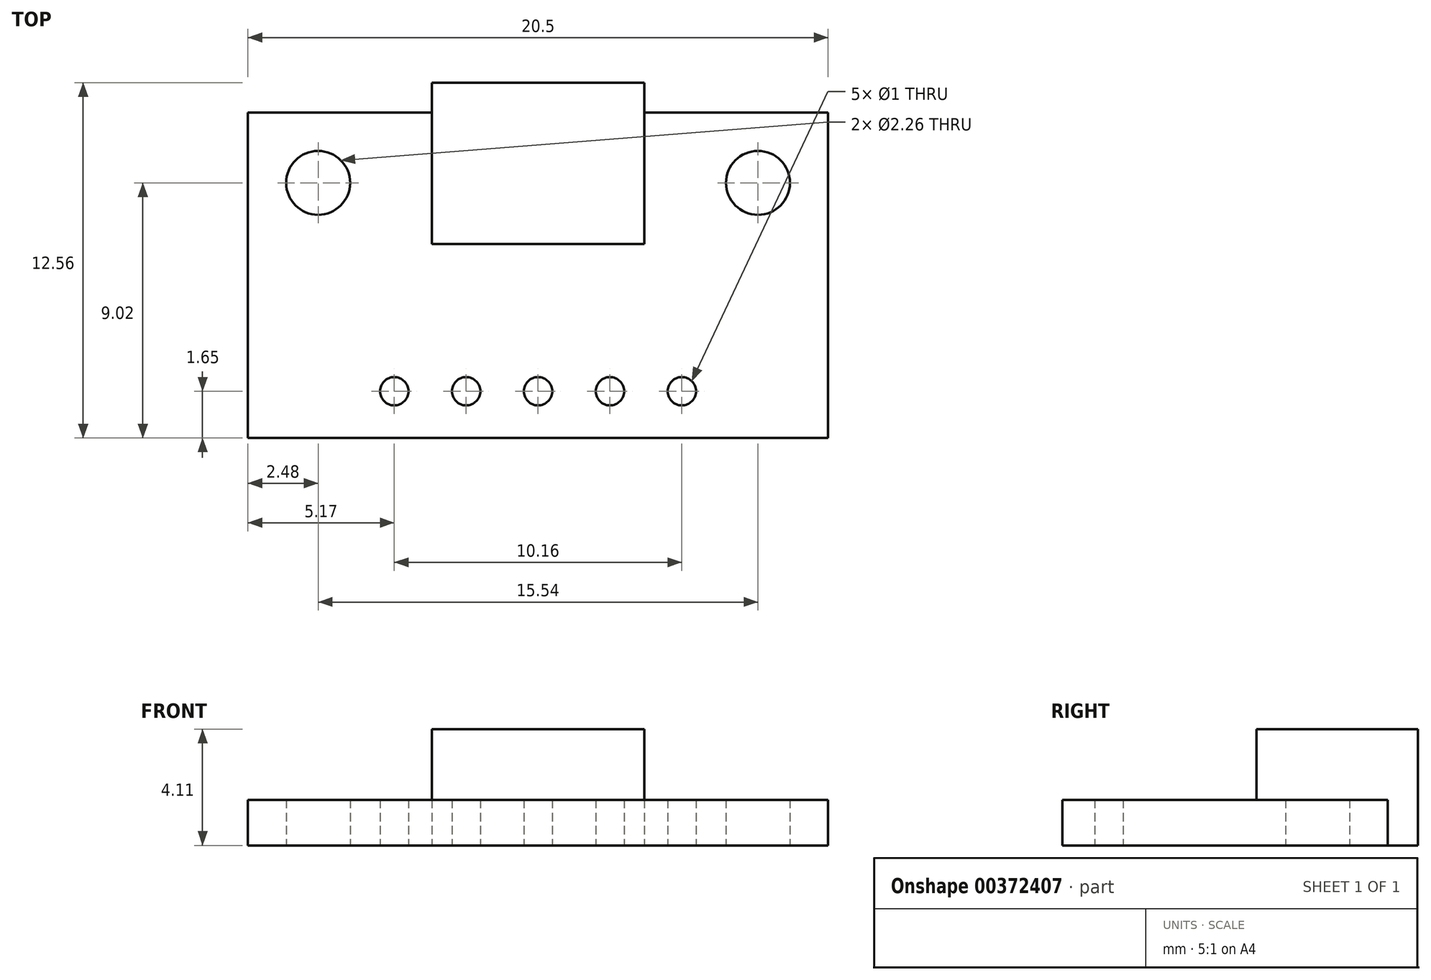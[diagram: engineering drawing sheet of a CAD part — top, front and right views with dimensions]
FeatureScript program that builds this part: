
annotation { "Feature Type Name" : "Feature", "Feature Type Description" : "" }
export const myFeature = defineFeature(function(context is Context, id is Id, definition is map)
    precondition{}
    {
        {
            var Q0;
            Q0=qCreatedBy(makeId("Top.planeOp"),FACE);
            var sketch = newSketch(context, id + "F0", { "sketchPlane" : qUnion([Q0])});
            skLineSegment(sketch, "E0.bottom", {"start": v(10.25, -5.75) * mm, "end": v(-10.25, -5.75) * mm});
            skLineSegment(sketch, "E0.top", {"start": v(10.25, 5.75) * mm, "end": v(-10.25, 5.75) * mm});
            skLineSegment(sketch, "E0.left", {"start": v(10.25, -5.75) * mm, "end": v(10.25, 5.75) * mm});
            skLineSegment(sketch, "E0.right", {"start": v(-10.25, -5.75) * mm, "end": v(-10.25, 5.75) * mm});
            skPoint(sketch, "E0.middle", {"position": v(0, 0) * mm});
            skLineSegment(sketch, "E1.bottom", {"start": v(-3.75, 6.8) * mm, "end": v(3.75, 6.8) * mm});
            skLineSegment(sketch, "E1.top", {"start": v(-3.75, 1.1) * mm, "end": v(3.75, 1.1) * mm});
            skLineSegment(sketch, "E1.left", {"start": v(-3.75, 6.81) * mm, "end": v(-3.75, 1.11) * mm});
            skLineSegment(sketch, "E1.right", {"start": v(3.75, 6.81) * mm, "end": v(3.75, 1.11) * mm});
            skPoint(sketch, "E2", {"position": v(0, 5.75) * mm});
            skPoint(sketch, "E3", {"position": v(0, 6.81) * mm});
            skCircle(sketch, "E4", {"center": v(0, -4.1) * mm, "radius": 0.5 * mm});
            skCircle(sketch, "E5.1.0.0", {"center": v(2.54, -4.1) * mm, "radius": 0.5 * mm});
            skCircle(sketch, "E5.2.0.0", {"center": v(5.08, -4.1) * mm, "radius": 0.5 * mm});
            skLineSegment(sketch, "E5.direction1", {"start": v(0, -4.1) * mm, "end": v(2.54, -4.1) * mm, "construction": true});
            skCircle(sketch, "E6.1.0.0", {"center": v(-2.54, -4.1) * mm, "radius": 0.5 * mm});
            skCircle(sketch, "E6.2.0.0", {"center": v(-5.08, -4.1) * mm, "radius": 0.5 * mm});
            skLineSegment(sketch, "E6.direction1", {"start": v(0, -4.1) * mm, "end": v(-2.54, -4.1) * mm, "construction": true});
            skCircle(sketch, "E7", {"center": v(-7.77, 3.27) * mm, "radius": 1.13 * mm});
            skCircle(sketch, "E8.MirrorC", {"center": v(7.77, 3.27) * mm, "radius": 1.13 * mm});
            skSolve(sketch);
        }
        {
            var Q0;
            Q0=makeQuery(id+"F0.imprint","IMPRINT",FACE,{"disambiguationData":[TD([[makeQuery(id+"F0.imprint","IMPRINT",EDGE,{"derivedFrom":sQuery(id+"F0.wireOp",EDGE,"E0.bottom")}),-1.0]])]});
            extrude(context, id + "F1", {"entities" : qUnion([Q0]), "depth" : 1.61 * mm});
        }
        {
            var Q0;
            {var subQ5=sQuery(id+"F0.wireOp",EDGE,"E1.top");Q0=makeQuery(id+"F0.imprint","IMPRINT",FACE,{"disambiguationData":[TD([[makeQuery(id+"F0.imprint","IMPRINT",EDGE,{"derivedFrom":subQ5}),1.0]])]});}
            var Q1;
            {var subQ5=sQuery(id+"F0.wireOp",EDGE,"E1.bottom");Q1=makeQuery(id+"F0.imprint","IMPRINT",FACE,{"disambiguationData":[TD([[makeQuery(id+"F0.imprint","IMPRINT",EDGE,{"derivedFrom":subQ5}),-1.0]])]});}
            extrude(context, id + "F2", {"entities" : qUnion([Q0, Q1]), "operationType" : NewBodyOperationType.ADD, "depth" : 4.11 * mm});
        }
    });
